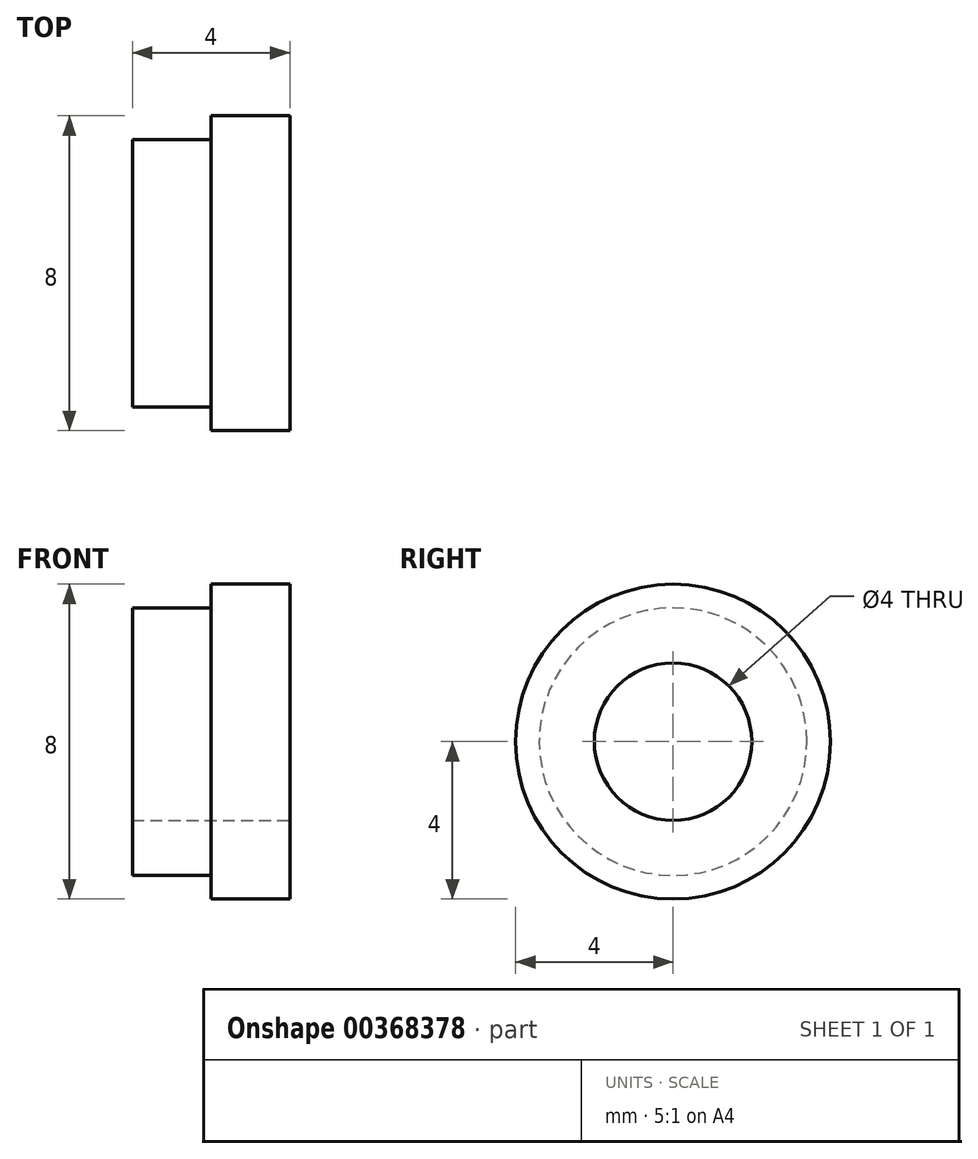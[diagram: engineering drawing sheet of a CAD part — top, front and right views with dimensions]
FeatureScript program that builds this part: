
annotation { "Feature Type Name" : "Feature", "Feature Type Description" : "" }
export const myFeature = defineFeature(function(context is Context, id is Id, definition is map)
    precondition{}
    {
        {
            var Q0;
            Q0=qCreatedBy(makeId("Top.planeOp"),FACE);
            var sketch = newSketch(context, id + "F0", { "sketchPlane" : qUnion([Q0])});
            skLineSegment(sketch, "E0", {"start": v(0, 3.4) * mm, "end": v(0, 2) * mm});
            skLineSegment(sketch, "E1", {"start": v(0, 2) * mm, "end": v(4, 2) * mm});
            skLineSegment(sketch, "E2", {"start": v(4, 2) * mm, "end": v(4, 4) * mm});
            skLineSegment(sketch, "E3", {"start": v(4, 4) * mm, "end": v(2, 4) * mm});
            skLineSegment(sketch, "E4", {"start": v(2, 4) * mm, "end": v(2, 3.4) * mm});
            skLineSegment(sketch, "E5", {"start": v(2, 3.4) * mm, "end": v(0, 3.4) * mm});
            skLineSegment(sketch, "E6", {"start": v(41.33, 0) * mm, "end": v(0, 0) * mm, "construction": true});
            skSolve(sketch);
        }
        {
            var Q0;
            Q0=qSketchRegion(id+"F0",true);
            var Q1;
            Q1=sQuery(id+"F0.wireOp",EDGE,"E6");
            revolve(context, id + "F1", {"entities" : qUnion([Q0]), "axis" : qUnion([Q1]), "revolveType" : RevolveType.FULL});
        }
    });
